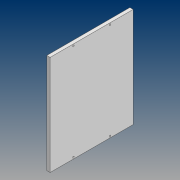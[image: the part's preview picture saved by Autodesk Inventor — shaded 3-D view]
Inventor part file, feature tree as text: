
AUTODESK INVENTOR PART (.ipt)
format: ipt  version: 2021 (Build 250183000, 183)  size: 97,792 bytes
history: native  units: mm
features: sketch x2, extrude x1, hole x1, mirror x1, projected_geometry x1
ambient origin geometry x8: Origin, YZ Plane, XZ Plane, XY Plane, X Axis, Y Axis, Z Axis, Center Point
bodies: Solid1 (feature_tree)
feature tree (6):
  extrude  "Extrusion1"  Depth=300.0mm
  hole  "Hole1"  [1 undecoded]
  mirror  "Mirror1"
  sketch  "Sketch1"  dims[d0=250.0mm d1=300.0mm]
  sketch  "Sketch2"  dims[d2=10.0mm d3=0.0mm d4=5.0mm d7=70.0mm d8=70.0mm d9=5.0mm d10=6.0mm d11=4.0mm d12=2.0mm d13=90.0deg d14=8.0mm d15=20.594885mm]
  projected_geometry  "Projected Loop1"
note: 1 required parameter value undecoded (feature->parameter linkage not recoverable at this tier; creation-order binding heuristic only, values carry confidence <= 0.55)
